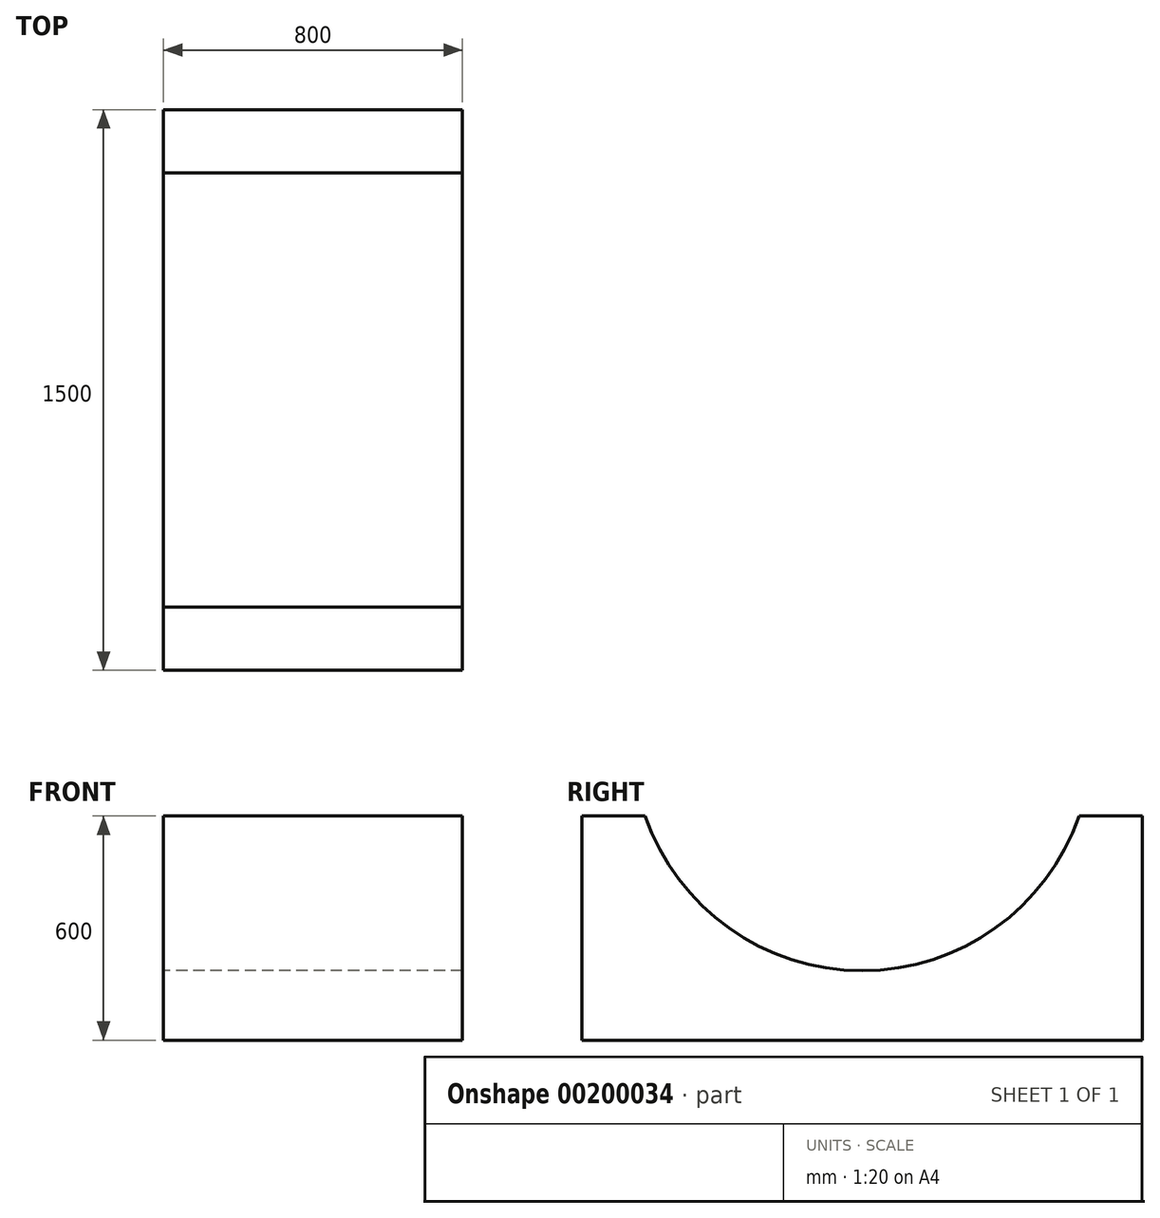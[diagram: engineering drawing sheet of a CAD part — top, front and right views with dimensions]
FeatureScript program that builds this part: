
annotation { "Feature Type Name" : "Feature", "Feature Type Description" : "" }
export const myFeature = defineFeature(function(context is Context, id is Id, definition is map)
    precondition{}
    {
        {
            var Q0;
            Q0=qCreatedBy(makeId("Top.planeOp"),FACE);
            var sketch = newSketch(context, id + "F0", { "sketchPlane" : qUnion([Q0])});
            skLineSegment(sketch, "E0.bottom", {"start": v(-400, 750) * mm, "end": v(400, 750) * mm});
            skLineSegment(sketch, "E0.top", {"start": v(-400, -750) * mm, "end": v(400, -750) * mm});
            skLineSegment(sketch, "E0.left", {"start": v(-400, 750) * mm, "end": v(-400, -750) * mm});
            skLineSegment(sketch, "E0.right", {"start": v(400, 750) * mm, "end": v(400, -750) * mm});
            skSolve(sketch);
        }
        {
            var Q0;
            Q0 = qSketchRegion(id + "F0", true);
            extrude(context, id + "F1", {"entities" : qUnion([Q0]), "depth" : 600 * mm});
        }
        {
            var Q0;
            Q0=makeQuery(id+"F1.opExtrude","SWEPT_FACE",FACE,{"disambiguationData":[OSD([sQuery(id+"F0.wireOp",EDGE,"E0.left")])]});
            var sketch = newSketch(context, id + "F2", { "sketchPlane" : qUnion([Q0])});
            skCircle(sketch, "E1", {"center": v(0, 800) * mm, "radius": 614.1 * mm});
            skSolve(sketch);
        }
        {
            var Q0;
            Q0 = qSketchRegion(id + "F2", true);
            extrude(context, id + "F3", {"entities" : qUnion([Q0]), "operationType" : NewBodyOperationType.REMOVE, "endBound" : BoundingType.THROUGH_ALL, "oppositeDirection" : true, "depth" : 25 * mm});
        }
    });
